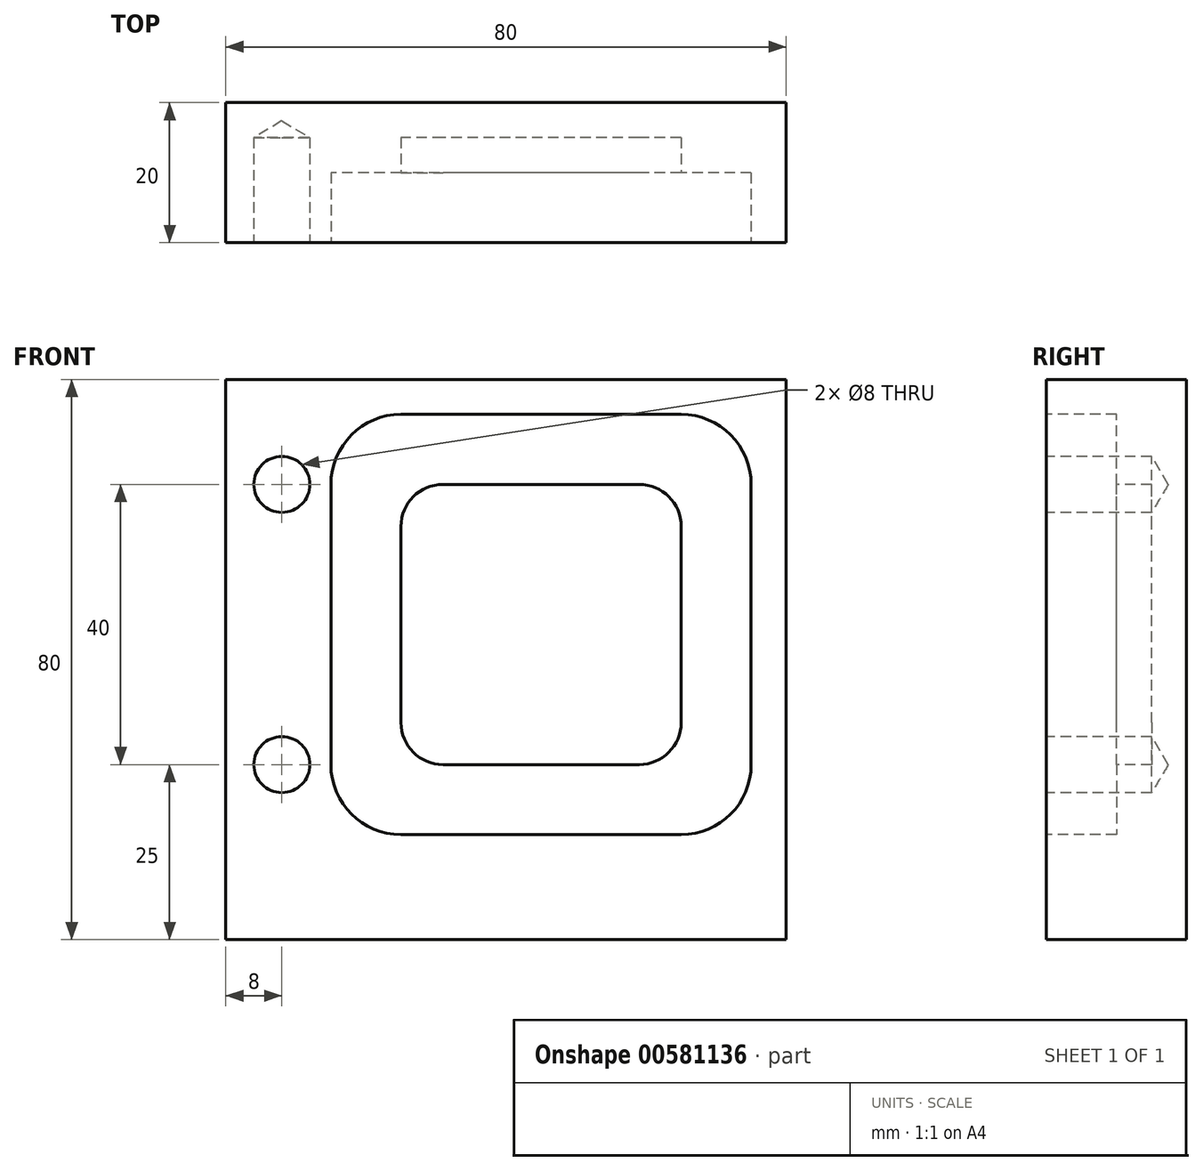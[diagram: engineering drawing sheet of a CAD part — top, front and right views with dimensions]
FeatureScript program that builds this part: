
annotation { "Feature Type Name" : "Feature", "Feature Type Description" : "" }
export const myFeature = defineFeature(function(context is Context, id is Id, definition is map)
    precondition{}
    {
        {
            var Q0;
            Q0=qCreatedBy(makeId("Front.planeOp"),FACE);
            var sketch = newSketch(context, id + "F0", { "sketchPlane" : qUnion([Q0])});
            skLineSegment(sketch, "E0.bottom", {"start": v(40, -40) * mm, "end": v(-40, -40) * mm});
            skLineSegment(sketch, "E0.top", {"start": v(40, 40) * mm, "end": v(-40, 40) * mm});
            skLineSegment(sketch, "E0.left", {"start": v(40, -40) * mm, "end": v(40, 40) * mm});
            skLineSegment(sketch, "E0.right", {"start": v(-40, -40) * mm, "end": v(-40, 40) * mm});
            skPoint(sketch, "E0.middle", {"position": v(0, 0) * mm});
            skSolve(sketch);
        }
        {
            var Q0;
            Q0=makeQuery(id+"F0.imprint","IMPRINT",FACE,{"disambiguationData":[TD([[makeQuery(id+"F0.imprint","IMPRINT",EDGE,{"derivedFrom":sQuery(id+"F0.wireOp",EDGE,"E0.bottom")}),-1.0]])]});
            extrude(context, id + "F1", {"entities" : qUnion([Q0]), "depth" : 20 * mm, "offsetDistance" : 25 * mm});
        }
        {
            var Q0;
            Q0=makeQuery(id+"F1.opExtrude","CAP_FACE",FACE,{"disambiguationData":[OSD([sQuery(id+"F0.wireOp",EDGE,"E0.bottom"),sQuery(id+"F0.wireOp",EDGE,"E0.top"),sQuery(id+"F0.wireOp",EDGE,"E0.left"),sQuery(id+"F0.wireOp",EDGE,"E0.right")])],"isStart":false});
            var sketch = newSketch(context, id + "F2", { "sketchPlane" : qUnion([Q0])});
            skCircle(sketch, "E1", {"center": v(-32, 25) * mm, "radius": 4 * mm});
            skCircle(sketch, "E2", {"center": v(-32, -15) * mm, "radius": 4 * mm});
            skSolve(sketch);
        }
        {
            var Q0;
            Q0=sQuery(id+"F2.wireOp",VERTEX,"E1.center");
            var Q1;
            Q1=sQuery(id+"F2.wireOp",VERTEX,"E2.center");
            var Q2;
            Q2=makeQuery(id+"F1.opExtrude","SWEPT_BODY",BODY,{"disambiguationData":[OSD([sQuery(id+"F0.wireOp",EDGE,"E0.bottom"),sQuery(id+"F0.wireOp",EDGE,"E0.top"),sQuery(id+"F0.wireOp",EDGE,"E0.left"),sQuery(id+"F0.wireOp",EDGE,"E0.right")])]});
            hole(context, id + "F3", {"style" : HoleStyle.SIMPLE, "endStyle" : HoleEndStyle.BLIND, "holeDiameter" : 8 * mm, "majorDiameter" : 5 * mm, "holeDepth" : 15 * mm, "isTappedThrough" : true, "tappedDepth" : 12 * mm, "tapClearance" : 3, "locations" : qUnion([Q0, Q1]), "scope" : qUnion([Q2])});
        }
        {
            var Q0;
            Q0=makeQuery(id+"F1.opExtrude","CAP_FACE",FACE,{"disambiguationData":[OSD([sQuery(id+"F0.wireOp",EDGE,"E0.bottom"),sQuery(id+"F0.wireOp",EDGE,"E0.top"),sQuery(id+"F0.wireOp",EDGE,"E0.left"),sQuery(id+"F0.wireOp",EDGE,"E0.right")])],"isStart":false});
            var sketch = newSketch(context, id + "F4", { "sketchPlane" : qUnion([Q0])});
            skPoint(sketch, "E3.middle", {"position": v(0, 0) * mm});
            skLineSegment(sketch, "E4.bottom", {"start": v(25, -25) * mm, "end": v(-15, -25) * mm});
            skLineSegment(sketch, "E4.top", {"start": v(25, 35) * mm, "end": v(-15, 35) * mm});
            skLineSegment(sketch, "E4.left", {"start": v(35, -15) * mm, "end": v(35, 25) * mm});
            skLineSegment(sketch, "E4.right", {"start": v(-25, -15) * mm, "end": v(-25, 25) * mm});
            skPoint(sketch, "E4.middle", {"position": v(5, 5) * mm});
            skPoint(sketch, "E5.visualSharp", {"position": v(-25, 35) * mm});
            skArc(sketch, "E5.filletArc", {"start": v(-15, 35) * mm, "mid": v(-22.07, 32.07) * mm, "end": v(-25, 25) * mm});
            skPoint(sketch, "E6.visualSharp", {"position": v(35, 35) * mm});
            skArc(sketch, "E6.filletArc", {"start": v(35, 25) * mm, "mid": v(32.07, 32.07) * mm, "end": v(25, 35) * mm});
            skPoint(sketch, "E7.visualSharp", {"position": v(35, -25) * mm});
            skArc(sketch, "E7.filletArc", {"start": v(25, -25) * mm, "mid": v(32.07, -22.07) * mm, "end": v(35, -15) * mm});
            skPoint(sketch, "E8.visualSharp", {"position": v(-25, -25) * mm});
            skArc(sketch, "E8.filletArc", {"start": v(-25, -15) * mm, "mid": v(-22.07, -22.07) * mm, "end": v(-15, -25) * mm});
            skLineSegment(sketch, "E9.bottom", {"start": v(19, -15) * mm, "end": v(-9, -15) * mm});
            skLineSegment(sketch, "E9.top", {"start": v(19, 25) * mm, "end": v(-9, 25) * mm});
            skLineSegment(sketch, "E9.left", {"start": v(25, -9) * mm, "end": v(25, 19) * mm});
            skLineSegment(sketch, "E9.right", {"start": v(-15, -9) * mm, "end": v(-15, 19) * mm});
            skArc(sketch, "E10.filletArc", {"start": v(-9, 25) * mm, "mid": v(-13.24, 23.24) * mm, "end": v(-15, 19) * mm});
            skArc(sketch, "E11.filletArc", {"start": v(25, 19) * mm, "mid": v(23.24, 23.24) * mm, "end": v(19, 25) * mm});
            skArc(sketch, "E12.filletArc", {"start": v(19, -15) * mm, "mid": v(23.24, -13.24) * mm, "end": v(25, -9) * mm});
            skArc(sketch, "E13.filletArc", {"start": v(-15, -9) * mm, "mid": v(-13.24, -13.24) * mm, "end": v(-9, -15) * mm});
            skSolve(sketch);
        }
        {
            var Q0;
            Q0=makeQuery(id+"F4.imprint","IMPRINT",FACE,{"disambiguationData":[TD([[makeQuery(id+"F4.imprint","IMPRINT",EDGE,{"derivedFrom":sQuery(id+"F4.wireOp",EDGE,"E4.bottom")}),-1.0]])]});
            extrude(context, id + "F5", {"entities" : qUnion([Q0]), "operationType" : NewBodyOperationType.REMOVE, "oppositeDirection" : true, "depth" : 10 * mm, "offsetDistance" : 25 * mm});
        }
        {
            var Q0;
            Q0=makeQuery(id+"F5.boolean.opBoolean","SPLIT",FACE,{"disambiguationData":[TD([makeQuery(id+"F5.opExtrude","SWEPT_FACE",FACE,{"disambiguationData":[OSD([sQuery(id+"F4.wireOp",EDGE,"E9.bottom")])]})])],"derivedFrom":makeQuery(id+"F1.opExtrude","CAP_FACE",FACE,{"disambiguationData":[OSD([sQuery(id+"F0.wireOp",EDGE,"E0.bottom"),sQuery(id+"F0.wireOp",EDGE,"E0.top"),sQuery(id+"F0.wireOp",EDGE,"E0.left"),sQuery(id+"F0.wireOp",EDGE,"E0.right")])],"isStart":false})});
            extrude(context, id + "F6", {"entities" : qUnion([Q0]), "operationType" : NewBodyOperationType.REMOVE, "oppositeDirection" : true, "depth" : 15 * mm, "offsetDistance" : 25 * mm});
        }
    });
